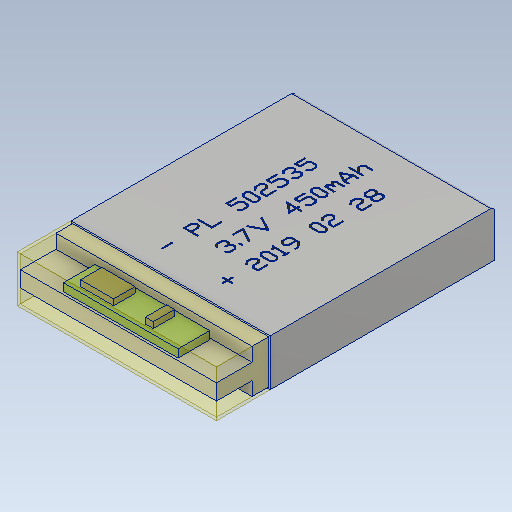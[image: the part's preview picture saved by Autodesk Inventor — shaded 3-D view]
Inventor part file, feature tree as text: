
AUTODESK INVENTOR PART (.ipt)
format: ipt  version: 2020.1 (Build 241239000, 239)  size: 659,456 bytes
history: native  units: mm
features: extrude x7, sketch x5, plane x1, emboss x1, fillet x1, projected_geometry x1
ambient origin geometry x8: Origin, YZ Plane, XZ Plane, XY Plane, X Axis, Y Axis, Z Axis, Center Point
bodies: Solid1 (feature_tree), Solid3 (feature_tree)
feature tree (16):
  sketch  "Sketch1"  dims[d1=35.0mm d2=4.5mm]
  extrude  "Extrusion1"  Depth=4.5mm
  extrude  "Extrusion2"  Depth=2.0mm TaperAngle=0.0deg
  plane  "Work Plane1"
  sketch  "Sketch3"  dims[d3=5.9mm d4=0.0mm d5=2.0mm d6=0.0mm]
  extrude  "Extrusion4"  Depth=25.0mm
  extrude  "Extrusion5"  Depth=0.2mm
  extrude  "Extrusion6"  Depth=10.0mm TaperAngle=0.0deg
  extrude  "Extrusion7"  Depth=0.2mm TaperAngle=0.0deg
  extrude  "Extrusion8"  Depth=14.5mm
  emboss  "Emboss1"
  fillet  "Fillet3"  Radius=4.0mm
  projected_geometry  "Projected Loop2"
  sketch  "Sketch4"  dims[d12=25.2mm d13=25.0mm]
  sketch  "Sketch5"  dims[d16=0.2mm d17=0.2mm]
  sketch  "Sketch6"  dims[d18=6.8mm d19=0.0mm d20=10.0mm d21=0.0mm d22=0.2mm d23=0.0mm d24=14.5mm d25=4.0mm d26=24.8mm d27=12.4mm d28=0.2mm d29=1.0mm d30=0.0mm d31=1.0mm d33=4.2mm d34=2.7mm d35=2.0mm d36=3.8mm d37=1.5mm d38=0.5mm d39=0.0mm d40=2.5mm d41=0.001mm d42=0.0mm d43=0.5mm]
